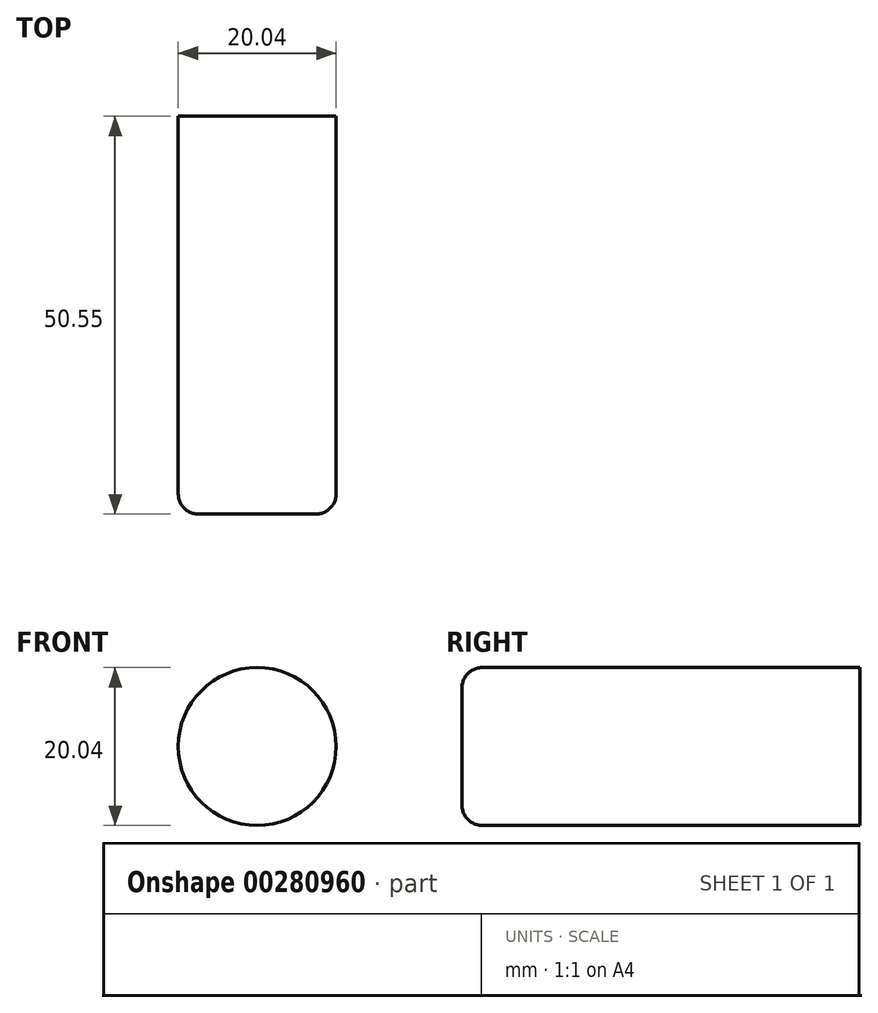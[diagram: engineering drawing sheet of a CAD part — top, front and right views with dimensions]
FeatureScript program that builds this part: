
annotation { "Feature Type Name" : "Feature", "Feature Type Description" : "" }
export const myFeature = defineFeature(function(context is Context, id is Id, definition is map)
    precondition{}
    {
        {
            var Q0;
            Q0=qCreatedBy(makeId("Front.planeOp"),FACE);
            var sketch = newSketch(context, id + "F0", { "sketchPlane" : qUnion([Q0])});
            skCircle(sketch, "E0", {"center": v(-54.8, 35.97) * mm, "radius": 10.02 * mm});
            skSolve(sketch);
        }
        {
            var Q0;
            Q0=makeQuery(id+"F0.imprint","IMPRINT",FACE,{"disambiguationData":[TD([[makeQuery(id+"F0.imprint","IMPRINT",EDGE,{"derivedFrom":sQuery(id+"F0.wireOp",EDGE,"E0")}),1.0]])]});
            extrude(context, id + "F1", {"entities" : qUnion([Q0]), "depth" : 50.55 * mm});
        }
        {
            var Q0;
            Q0=makeQuery(id+"F1.opExtrude","CAP_EDGE",EDGE,{"disambiguationData":[OSD([sQuery(id+"F0.wireOp",EDGE,"E0")])],"isStart":false});
            fillet(context, id + "F2", {"entities" : qUnion([Q0]), "radius" : 2.54 * mm, "tangentPropagation" : true, "allowEdgeOverflow" : false});
        }
        {
            var Q0;
            Q0=qCreatedBy(makeId("Front.planeOp"),FACE);
            var sketch = newSketch(context, id + "F3", { "sketchPlane" : qUnion([Q0])});
            skCircle(sketch, "E1", {"center": v(-54.8, 36.26) * mm, "radius": 2.9 * mm});
            skSolve(sketch);
        }
        {
            var Q0;
            Q0=sQuery(id+"F3.wireOp",EDGE,"E1");
            extrude(context, id + "F4", {"bodyType" : ToolBodyType.SURFACE, "surfaceEntities" : qUnion([Q0]), "depth" : 54.86 * mm});
        }
    });
